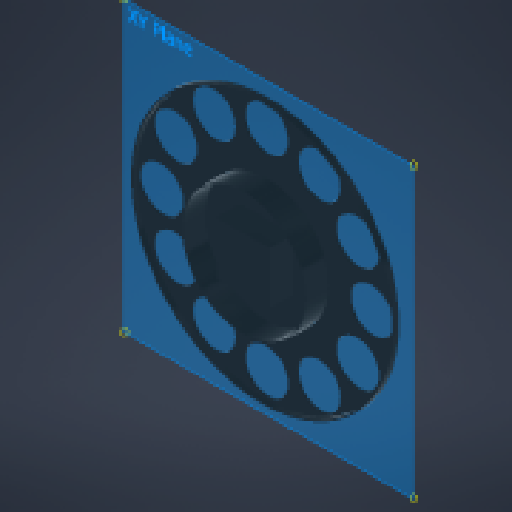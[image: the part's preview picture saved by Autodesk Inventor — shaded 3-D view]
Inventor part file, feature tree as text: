
AUTODESK INVENTOR PART (.ipt)
format: ipt  version: 2023.1 (Build 271208000, 208)  size: 3,852,800 bytes
history: native  units: mm
features: sketch x5, extrude x3, other x1
ambient origin geometry x8: Origin, YZ Plane, XZ Plane, XY Plane, X Axis, Y Axis, Z Axis, Center Point
bodies: Solid1 (feature_tree)
feature tree (9):
  extrude  "Extrusion1"  Depth=50.0mm
  extrude  "Extrusion2"  Depth=120.0mm
  extrude  "Extrusion3"  Depth=2.0mm TaperAngle=0.0deg
  sketch  "Sketch4"  dims[d10=2.0mm]
  sketch  "Sketch5"  dims[d11=5.0mm d12=0.0mm d13=142.0mm d14=1.0mm d15=26.0mm d16=0.0mm d17=60.0mm d18=60.0mm]
  sketch  "Sketch1"  dims[d0=300.0mm d1=50.0mm]
  sketch  "Sketch2"  dims[d2=0.0mm d3=120.0mm]
  sketch  "Sketch3"  dims[d4=120.0mm d6=360.0deg d8=2.0mm d9=0.0mm]
  other  "Image1"
